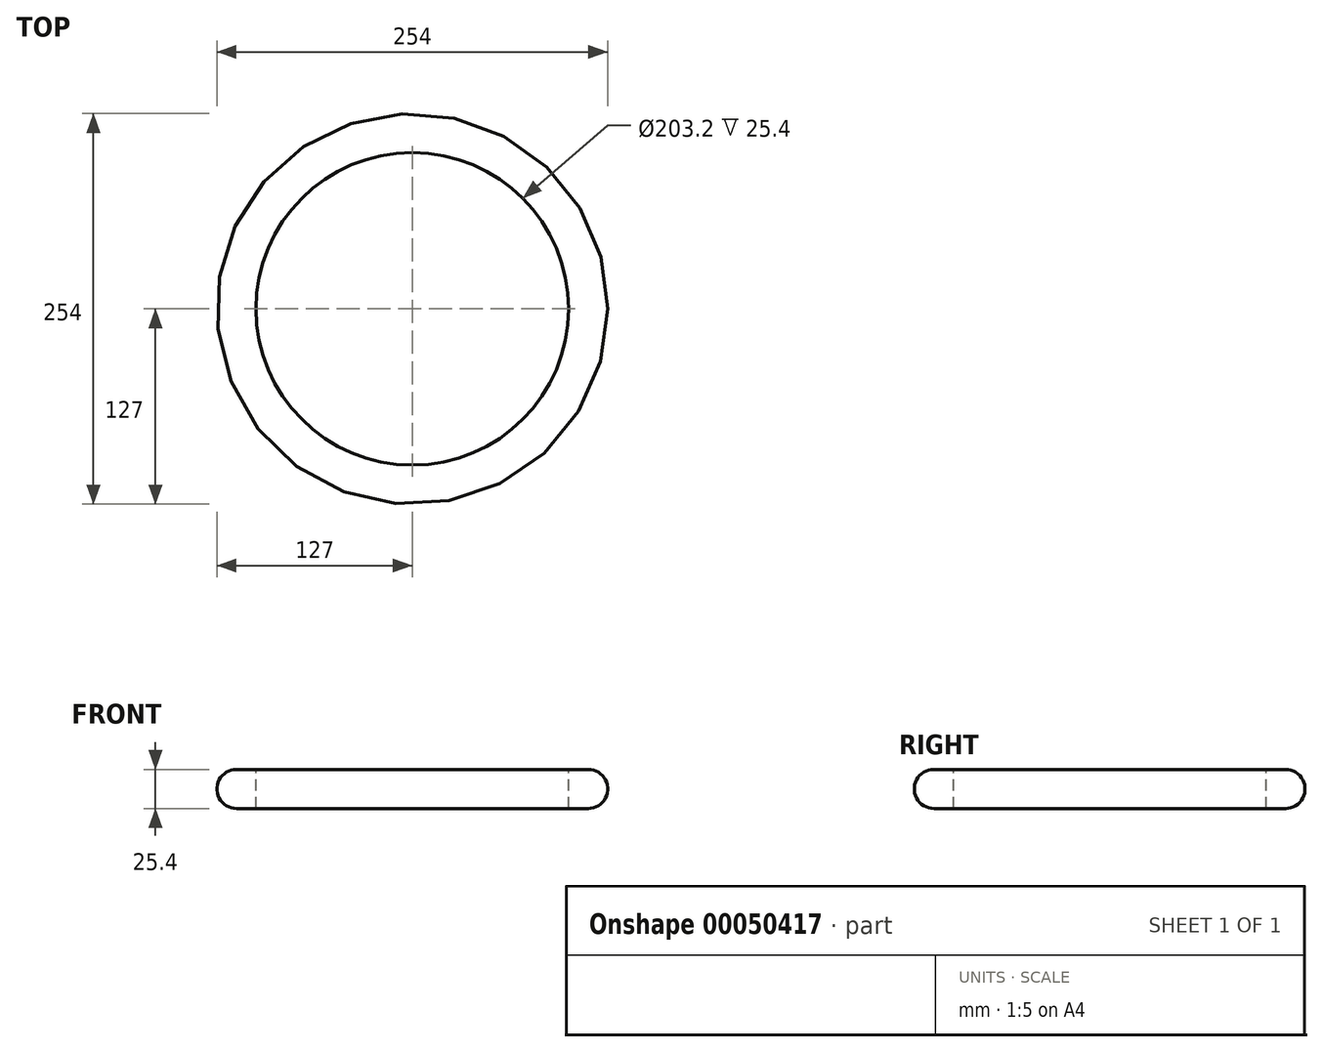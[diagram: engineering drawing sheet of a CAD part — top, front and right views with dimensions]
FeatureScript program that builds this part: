
annotation { "Feature Type Name" : "Feature", "Feature Type Description" : "" }
export const myFeature = defineFeature(function(context is Context, id is Id, definition is map)
    precondition{}
    {
        {
            var Q0;
            Q0=qCreatedBy(makeId("Top.planeOp"),FACE);
            var sketch = newSketch(context, id + "F0", { "sketchPlane" : qUnion([Q0])});
            skCircle(sketch, "E0", {"center": v(0, 0) * mm, "radius": 101.6 * mm});
            skCircle(sketch, "E1", {"center": v(0, 0) * mm, "radius": 127 * mm});
            skSolve(sketch);
        }
        {
            var Q0;
            Q0=makeQuery(id+"F0.imprint","IMPRINT",FACE,{"disambiguationData":[TD([[makeQuery(id+"F0.imprint","IMPRINT",EDGE,{"derivedFrom":sQuery(id+"F0.wireOp",EDGE,"E0")}),-1.0]])]});
            extrude(context, id + "F1", {"entities" : qUnion([Q0]), "oppositeDirection" : true, "depth" : 25.4 * mm});
        }
        {
            var Q0;
            Q0=makeQuery(id+"F1.opExtrude","CAP_EDGE",EDGE,{"disambiguationData":[OSD([sQuery(id+"F0.wireOp",EDGE,"E1")])],"isStart":true});
            var Q1;
            Q1=makeQuery(id+"F1.opExtrude","CAP_EDGE",EDGE,{"disambiguationData":[OSD([sQuery(id+"F0.wireOp",EDGE,"E1")])],"isStart":false});
            fillet(context, id + "F2", {"entities" : qUnion([Q0, Q1]), "radius" : 12.7 * mm, "tangentPropagation" : true, "allowEdgeOverflow" : false});
        }
    });
